# Revit family: QF_MARCO_1001945US_POUR'D_TOUCH_CONTROL_BOX
name_source: partatom
category: Specialty Equipment
units: mm (PartAtom-declared; Revit-internal decimal feet)

## family parameters
Always vertical = Yes
Cut with Voids When Loaded = No
Enable Cutting in Views = No
Maintain Annotation Orientation = No
Part Type = Normal
Room Calculation Point = No
Round Connector Dimension = Use Diameter
Shared = No
Work Plane-Based = No

## types (1)
- QF_MARCO_1001945US_POUR'D_TOUCH_CONTROL_BOX
    Apparent Power = 0 VA
    Conn Conduit = Yes
    Cycle = 0 Hz
    Default Elevation = 0 "
    Depth = 15.06 "
    Description = POUR'D TOUCH CONTROL BOX
    Elec Conn Connection Height = 0 "
    Elec Conn RI Height = 0 "
    FL Amps = 0 A
    Foodservice Equipment Identifier = Yes
    Height = 5.5 "
    Identify Quantity as Lot = Yes
    Length = 6.2 "
    Manufacturer = MARCO
    Max Overcurrent Protection = 0 A
    Min Ckt Ampacity = 0 A
    Model = 1001945US
    Number of Poles = 1
    Phase = 0
    Volts = 0 V
    Watts = 0 W
    Weight in Pounds = 0

## geometry (parser evidence)
native form markers: Sweep x6
no freeform markers — native parametric forms only
